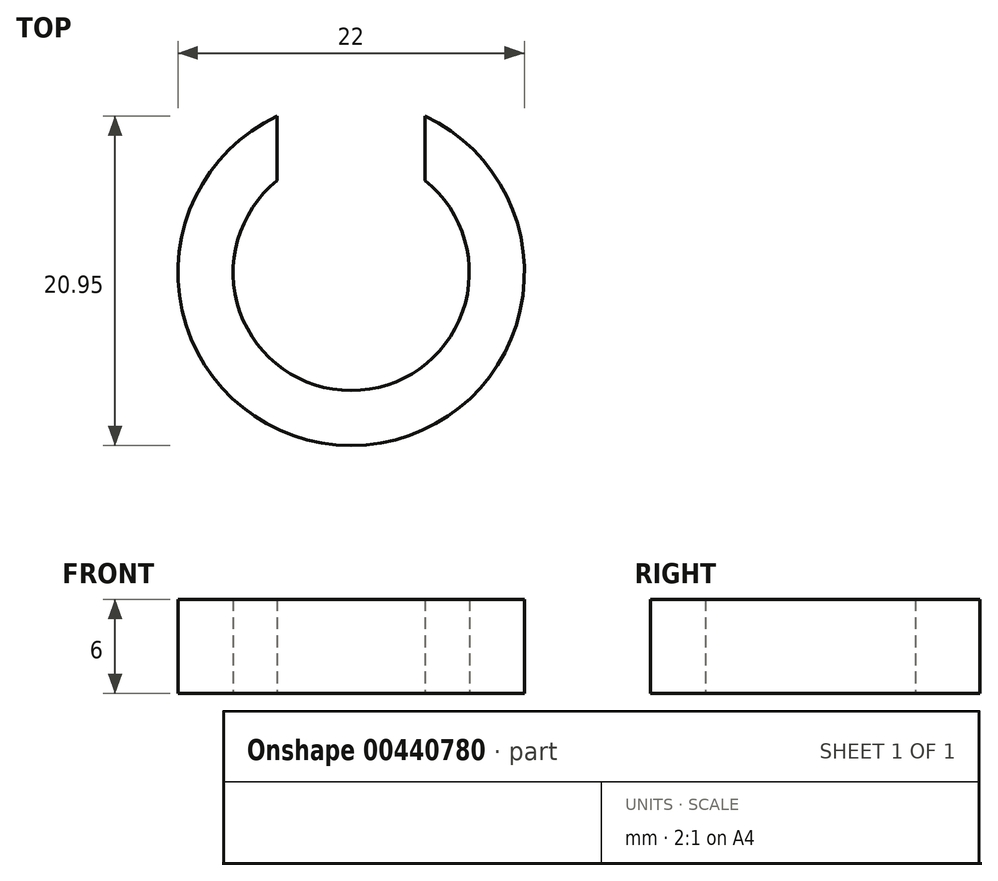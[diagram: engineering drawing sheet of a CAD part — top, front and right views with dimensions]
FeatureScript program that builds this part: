
annotation { "Feature Type Name" : "Feature", "Feature Type Description" : "" }
export const myFeature = defineFeature(function(context is Context, id is Id, definition is map)
    precondition{}
    {
        {
            var Q0;
            Q0=qCreatedBy(makeId("Top.planeOp"),FACE);
            var sketch = newSketch(context, id + "F0", { "sketchPlane" : qUnion([Q0])});
            skCircle(sketch, "E0", {"center": v(0, 0) * mm, "radius": 11 * mm});
            skCircle(sketch, "E1", {"center": v(0, 0) * mm, "radius": 7.5 * mm});
            skSolve(sketch);
        }
        {
            var Q0;
            Q0=makeQuery(id+"F0.imprint","IMPRINT",FACE,{"disambiguationData":[TD([[makeQuery(id+"F0.imprint","IMPRINT",EDGE,{"derivedFrom":sQuery(id+"F0.wireOp",EDGE,"E0")}),1.0]])]});
            extrude(context, id + "F1", {"entities" : qUnion([Q0]), "depth" : 6 * mm});
        }
        {
            var Q0;
            Q0=qCreatedBy(makeId("Front.planeOp"),FACE);
            var sketch = newSketch(context, id + "F2", { "sketchPlane" : qUnion([Q0])});
            skLineSegment(sketch, "E2.bottom", {"start": v(-4.7, 13.9) * mm, "end": v(4.7, 13.9) * mm});
            skLineSegment(sketch, "E2.top", {"start": v(-4.7, -6.33) * mm, "end": v(4.7, -6.33) * mm});
            skLineSegment(sketch, "E2.left", {"start": v(-4.7, 13.9) * mm, "end": v(-4.7, -6.33) * mm});
            skLineSegment(sketch, "E2.right", {"start": v(4.7, 13.9) * mm, "end": v(4.7, -6.33) * mm});
            skSolve(sketch);
        }
        {
            var Q0;
            Q0=makeQuery(id+"F2.imprint","IMPRINT",FACE,{"disambiguationData":[TD([[makeQuery(id+"F2.imprint","IMPRINT",EDGE,{"derivedFrom":sQuery(id+"F2.wireOp",EDGE,"E2.bottom")}),-1.0]])]});
            extrude(context, id + "F3", {"entities" : qUnion([Q0]), "operationType" : NewBodyOperationType.REMOVE, "oppositeDirection" : true, "depth" : 25 * mm});
        }
    });
